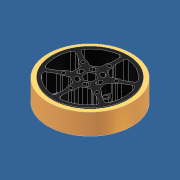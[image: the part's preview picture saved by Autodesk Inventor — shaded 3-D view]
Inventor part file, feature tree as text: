
AUTODESK INVENTOR PART (.ipt)
format: ipt  version: unknown  size: 610,304 bytes
history: native  units: in
note: dims shown in document units (in); Inventor stores cm internally (conversion verified against a paired STEP export)
features: other x1, imported_body x1, extrude x1, sketch x1
ambient origin geometry x8: Origin, YZ Plane, XZ Plane, XY Plane, X Axis, Y Axis, Z Axis, Center Point
feature tree (4):
  other  "Cut-Extrude9"
  imported_body  "Base1"
  extrude  "Extrusion1"  Depth=1.0in TaperAngle=0.0deg
  sketch  "Sketch1"  dims[d0=0.2in d1=1.0in d2=0.0in]
